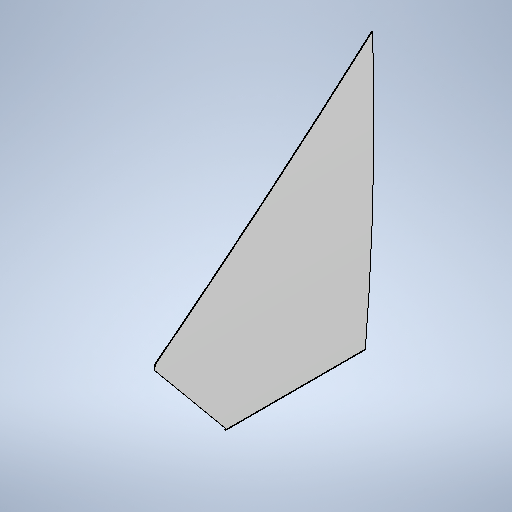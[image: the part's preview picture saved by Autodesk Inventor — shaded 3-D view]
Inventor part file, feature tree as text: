
AUTODESK INVENTOR PART (.ipt)
format: ipt  version: 2025 (Build 290162010, 162A)  size: 468,480 bytes
history: native  units: mm
features: other x4, sheet_metal_op x3, sketch x3, projected_geometry x2, extrude x1
ambient origin geometry x8: Origin, YZ Plane, XZ Plane, XY Plane, X Axis, Y Axis, Z Axis, Center Point
bodies: Body1 (feature_tree)
feature tree (13):
  sheet_metal_op  "Contour Flange2"
  extrude  "Extrusion2"  Depth=3.0mm
  other  "Mark4"
  other  "A-Side Definition"
  sketch  "Sketch1"  dims[d36=3.0mm d37=3.0mm]
  other  "Plate2"
  sheet_metal_op  "Bend2"
  sheet_metal_op  "Corner2"
  sketch  "Sketch2"  dims[d38=1.5mm]
  projected_geometry  "Projected Loop5"
  projected_geometry  "Projected Loop6"
  sketch  "Sketch6"  dims[d39=6.0mm d40=5.0mm d41=980.0mm d42=5.0mm d43=3.0mm d44=12.0mm d45=3.0mm d46=5.0mm d65=8.0mm d78=3.0mm d80=3.0mm d123=0.0mm d124=0.0mm d153=5.0mm d154=63.0mm d155=11050.0mm d156=23.736478mm d158=5.0mm d160=300.0mm d162=6.981317mm d163=6.981317mm d172=578.0mm d174=1843.0mm d175=0.0mm d176=1.0mm]
  other  "Definition1"
